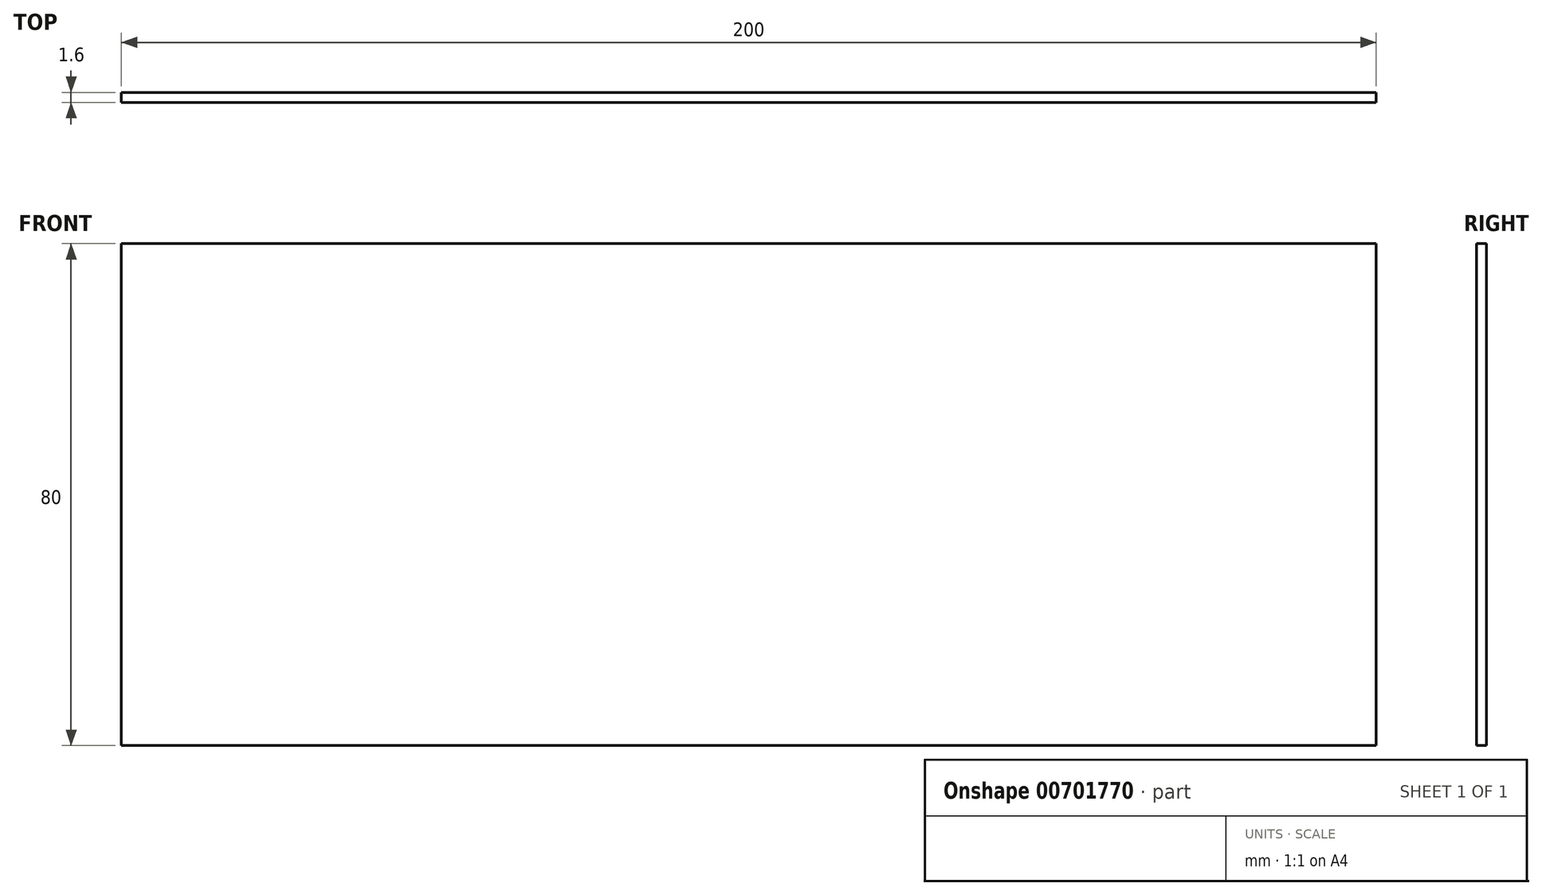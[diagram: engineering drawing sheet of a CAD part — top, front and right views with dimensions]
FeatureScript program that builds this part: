
annotation { "Feature Type Name" : "Feature", "Feature Type Description" : "" }
export const myFeature = defineFeature(function(context is Context, id is Id, definition is map)
    precondition{}
    {
        {
            var Q0;
            Q0=qCreatedBy(makeId("Front.planeOp"),FACE);
            var sketch = newSketch(context, id + "F0", { "sketchPlane" : qUnion([Q0])});
            skLineSegment(sketch, "E0.bottom", {"start": v(-100, 40) * mm, "end": v(100, 40) * mm});
            skLineSegment(sketch, "E0.top", {"start": v(-100, -40) * mm, "end": v(100, -40) * mm});
            skLineSegment(sketch, "E0.left", {"start": v(-100, 40) * mm, "end": v(-100, -40) * mm});
            skLineSegment(sketch, "E0.right", {"start": v(100, 40) * mm, "end": v(100, -40) * mm});
            skPoint(sketch, "E0.middle", {"position": v(0, 0) * mm});
            skLineSegment(sketch, "E1", {"start": v(-100, 0) * mm, "end": v(100, 0) * mm, "construction": true});
            skPoint(sketch, "E2", {"position": v(95, 0) * mm});
            skPoint(sketch, "E3", {"position": v(48.5, 0) * mm});
            skPoint(sketch, "E4", {"position": v(2, 0) * mm});
            skPoint(sketch, "E5", {"position": v(-44.5, 0) * mm});
            skPoint(sketch, "E6", {"position": v(-91, 0) * mm});
            skSolve(sketch);
        }
        {
            var Q0;
            Q0=makeQuery(id+"F0.imprint","IMPRINT",FACE,{"disambiguationData":[TD([[makeQuery(id+"F0.imprint","IMPRINT",EDGE,{"derivedFrom":sQuery(id+"F0.wireOp",EDGE,"E0.bottom")}),-1.0]])]});
            extrude(context, id + "F1", {"entities" : qUnion([Q0]), "oppositeDirection" : true, "depth" : 1.6 * mm});
        }
    });
